# Revit family: Basin-Drop In-Caroma Grace 50 Vanity1
name_source: partatom
category: Plumbing Fixtures
revit_build: Autodesk Revit 2014 (Build: 20131024_2115(x64)
units: mm (PartAtom-declared; Revit-internal decimal feet)

## types (1)
- Grace 565 - 0 Tap Holes
    1 Taphole = No
    3 Tapholes = No
    Assembly Code = D2010310
    CW Connection = No
    Capacity_ANZRS = 13.3 L
    Cost = 0 $
    Default Elevation = 0 mm  [stored 0 ft]
    Description = Caroma Grace 565 Vanity Basin
    HW Connection = No
    Height_ANZRS = 160 mm  [stored 0.524934 ft]
    Keynote = HB
    Length_ANZRS = 565 mm  [stored 1.85367 ft]
    Manufacturer = GWA Bathrooms & Kitchens
    Material_ANZRS = Porcelain-White-Caroma
    Model = EU8032A00
    ModifiedIssue_ANZRS = 20141029.01 $
    PlumbingMaterial_ANZRS = PVC-White-Caroma
    Spout Penetration = 100 mm  [stored 0.328084 ft]
    Tap Penetrations = 100 mm  [stored 0.328084 ft]
    Type Comments = Overflow available only, White plug and chrome flush fitting waste included
    URL = http://www.caroma.com.au
    Vent Connection = No
    WFU = 2
    Waste = Metal-Chrome-Caroma
    Waste Connection = Yes
    WasteOutlet_ANZRS = 0
    Width_ANZRS = 395 mm  [stored 1.29593 ft]

note: [stored X ft] marks values corroborated as IEEE doubles in the binary element streams (Revit-internal decimal feet)

## geometry (parser evidence)
native form markers: Blend x14, Sweep x1
no freeform markers — native parametric forms only
